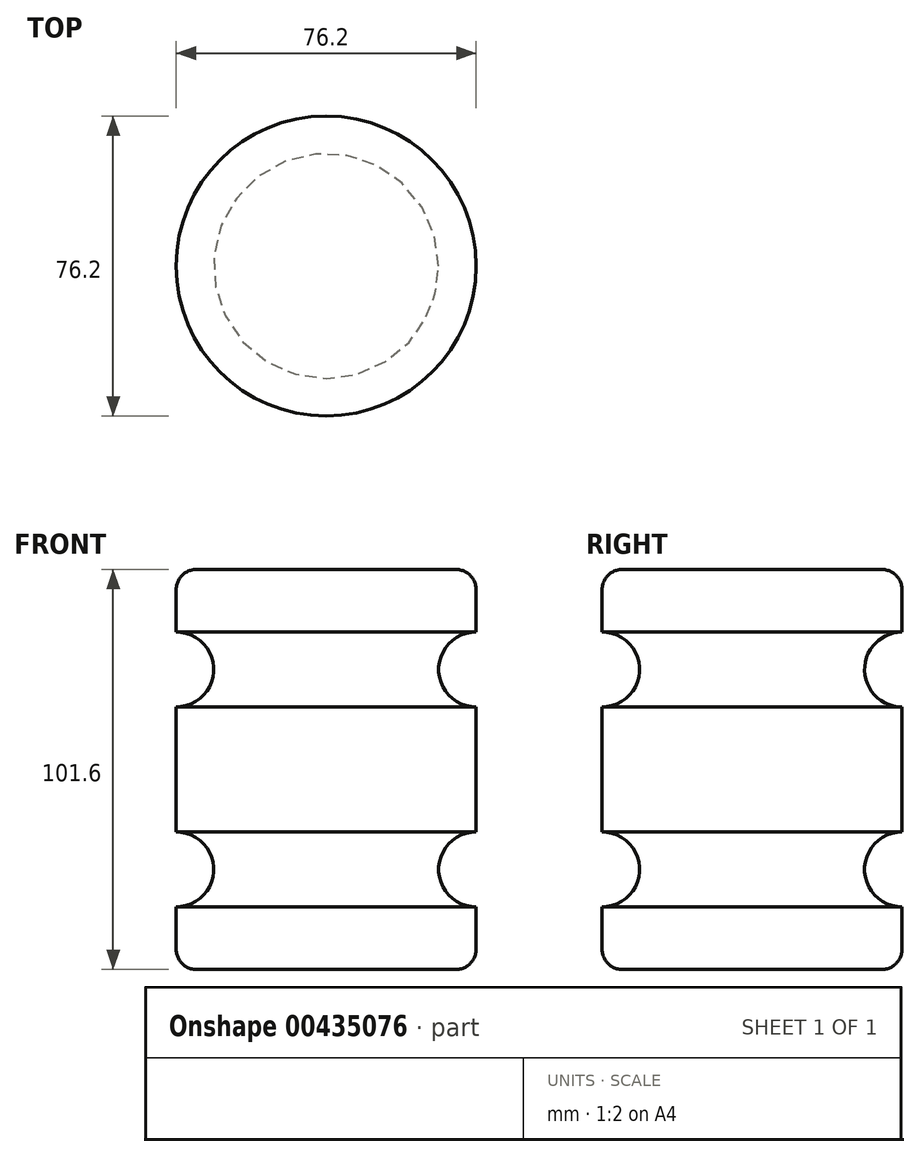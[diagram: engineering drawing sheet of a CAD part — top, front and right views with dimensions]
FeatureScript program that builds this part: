
annotation { "Feature Type Name" : "Feature", "Feature Type Description" : "" }
export const myFeature = defineFeature(function(context is Context, id is Id, definition is map)
    precondition{}
    {
        {
            var Q0;
            Q0=qCreatedBy(makeId("Front.planeOp"),FACE);
            var sketch = newSketch(context, id + "F0", { "sketchPlane" : qUnion([Q0])});
            skLineSegment(sketch, "E0.bottom", {"start": v(-32.03, 76.82) * mm, "end": v(6.07, 76.82) * mm});
            skLineSegment(sketch, "E0.top", {"start": v(-32.03, -24.78) * mm, "end": v(6.07, -24.78) * mm});
            skLineSegment(sketch, "E0.left", {"start": v(-32.03, 76.82) * mm, "end": v(-32.03, -24.78) * mm});
            skLineSegment(sketch, "E0.right", {"start": v(6.07, 76.82) * mm, "end": v(6.07, 60.94) * mm});
            skArc(sketch, "E1", {"start": v(6.07, 60.94) * mm, "mid": v(-3.46, 51.42) * mm, "end": v(6.07, 41.9) * mm});
            skArc(sketch, "E2", {"start": v(6.07, 10.14) * mm, "mid": v(-3.46, 0.62) * mm, "end": v(6.07, -8.9) * mm});
            skLineSegment(sketch, "E3.trimOffspring", {"start": v(6.07, -8.9) * mm, "end": v(6.07, -24.78) * mm});
            skLineSegment(sketch, "E4.trimOffspring", {"start": v(6.07, 41.9) * mm, "end": v(6.07, 10.14) * mm});
            skSolve(sketch);
        }
        {
            var Q0;
            Q0=makeQuery(id+"F0.imprint","IMPRINT",FACE,{"disambiguationData":[TD([[makeQuery(id+"F0.imprint","IMPRINT",EDGE,{"derivedFrom":sQuery(id+"F0.wireOp",EDGE,"E0.bottom")}),-1.0]])]});
            var Q1;
            Q1=sQuery(id+"F0.wireOp",EDGE,"E0.left");
            revolve(context, id + "F1", {"entities" : qUnion([Q0]), "axis" : qUnion([Q1]), "revolveType" : RevolveType.FULL});
        }
        {
            var Q0;
            Q0=makeQuery(id+"F1.opRevolve","SWEPT_EDGE",EDGE,{"disambiguationData":[OSD([sQuery(id+"F0.wireOp",EDGE,"E0.bottom"),sQuery(id+"F0.wireOp",EDGE,"E0.right")])]});
            var Q1;
            Q1=makeQuery(id+"F1.opRevolve","SWEPT_EDGE",EDGE,{"disambiguationData":[OSD([sQuery(id+"F0.wireOp",EDGE,"E0.top"),sQuery(id+"F0.wireOp",EDGE,"E3.trimOffspring")])]});
            fillet(context, id + "F2", {"entities" : qUnion([Q0, Q1]), "radius" : 5.08 * mm, "tangentPropagation" : true, "allowEdgeOverflow" : false});
        }
    });
